# Revit family: NBS_TapcoRoofingProducts_DryFxngRdgs_RidgeMasterPlus
name_source: partatom
category: Generic Models
units: mm (PartAtom-declared; Revit-internal decimal feet)

## family parameters
Can host rebar = No
Cut with Voids When Loaded = No
Part Type = Normal
Room Calculation Point = No
Round Connector Dimension = Use Diameter
Shared = No

## types (1)
- RidgeMasterPlus
    Applications = Suitable for use with TapcoSlate Classic Ridge/ Hip system, for roof pitches 14 to 45 degrees
    AssetType = Fixed
    BIMObjectName = NBS_TapcoRoofingProducts_DryFixingRidges_RidgeMasterPlus
    Category = Pr_35_90_93_29:Dry fixing ridges
    Color = Black
    Combustible = Yes
    Description = A dry-fix ridge ventilation system that fits underneath the TapcoSlate Classic Ridge/ Hip system
    DurationUnit = year
    ExpectedLife = 50+ years
    Features = A patented added-pitch design reduces the visibility of the vent opening, patented internal baffle system engineered to keep blowing rain and snow from getting in, internal filter blocks out insects, leaves and other debris, easily adapts to a peak vent or flash vent, nailing supports and structural ribs make the Ridge Master Plus crushproof, self-aligning, interlocking ends make it easy to install correctly, built-in end caps adjust to the roof pitch while the ship-lap design allows for expansion and contraction as temperatures change, can be joined with Hip Master hip ventilation, 10 000 mm²/m ventilation provision to comply with building regulations for both warm and cold roofs
    IfcExportAs = IfcCoveringType
    IfcExportType = ROOFING
    IsExternal = Yes
    ManufacturerName = Tapco Roofing Products
    ManufacturerURL = www.tapcoroofingproducts.com
    Material = Polypropylene (PP) and Rubber
    ModelReference = RidgeMasterPlus
    NBSCertification = www.nationalbimlibrary.com/cert/gkjmcfqb
    NBSDescription = Dry fixing ridges
    NBSReference = 45-80-90/376
    Name = DryFixingRidges_RidgeMasterPlus_TapcoRoofingProducts
    NominalHeight = 35 mm  [stored 0.114829 ft]
    NominalLength = 1219 mm
    NominalWidth = 270 mm
    PitchRange = 14° - 45°
    ProductInformation = https://www.tapcoroofingproducts.com
    RidgeMaterial = NBS_TapcoRoofingProducts_Polypropylene_Black
    Size = 1219 x 270 x 35 mm
    Status = UNSET
    ThermalTransmittance = 0
    Uniclass2015Code = Pr_35_90_93_29
    Uniclass2015Title = Dry fixing ridges
    Uniclass2015Version = Products v1.20
    Version = 1
    WarrantyDescription = 40-years
    WarrantyDurationUnit = year

note: [stored X ft] marks values corroborated as IEEE doubles in the binary element streams (Revit-internal decimal feet)

## geometry (parser evidence)
native form markers: Sweep x3
no freeform markers — native parametric forms only
